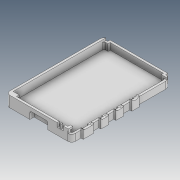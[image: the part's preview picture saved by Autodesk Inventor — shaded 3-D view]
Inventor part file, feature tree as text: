
AUTODESK INVENTOR PART (.ipt)
format: ipt  version: 2020 (Build 240168000, 168)  size: 389,120 bytes
history: native  units: mm
features: extrude x11, sketch x10
ambient origin geometry x8: Origin, YZ Plane, XZ Plane, XY Plane, X Axis, Y Axis, Z Axis, Center Point
bodies: Solid1 (feature_tree)
feature tree (21):
  extrude  "Extrusion1"  Depth=60.0mm
  extrude  "Extrusion2"  Depth=2.0mm
  extrude  "Extrusion3"  Depth=2.0mm TaperAngle=0.0deg
  extrude  "Extrusion4"  Depth=9.6mm
  extrude  "Extrusion5"  Depth=1.0mm
  extrude  "Extrusion6"  Depth=6.7mm
  extrude  "Extrusion7"  Depth=1.5mm
  extrude  "Extrusion8"  Depth=6.7mm
  extrude  "Extrusion12"  Depth=1.0mm
  sketch  "Sketch12"  dims[d19=7.6mm d20=6.7mm d21=9.0mm d22=8.0mm d23=2.0mm d24=0.0mm d25=2.0mm d27=2.0mm d28=2.5mm d29=2.5mm d30=2.5mm d31=5.5mm d32=4.3mm d33=0.0mm d35=2.0mm d36=2.0mm d37=6.0mm d38=0.0mm d39=2.0mm d40=8.0mm d41=0.0mm d42=7.5mm d43=4.5mm d44=1.5mm d45=0.0mm d46=2.3mm d47=4.2mm d48=4.2mm d49=2.0mm d50=3.0mm d51=1.5mm d52=0.0mm d53=2.3mm d55=2.3mm d56=1.0mm d57=2.3mm d58=1.5mm d59=0.0mm d71=6.8mm d72=16.4mm d73=1.5mm d74=3.8mm d75=0.0mm d76=1.0mm d77=4.8mm d78=2.0mm d79=0.0mm d80=3.0mm d81=0.0mm]
  extrude  "Extrusion13"  Depth=6.7mm
  extrude  "Extrusion14"  Depth=3.0mm
  sketch  "Sketch1"  dims[d0=89.7mm d1=60.0mm]
  sketch  "Sketch2"  dims[d2=3.5mm d3=2.0mm]
  sketch  "Sketch3"  dims[d4=52.8mm d5=2.0mm d6=0.0mm]
  sketch  "Sketch4"  dims[d7=8.0mm d8=9.6mm]
  sketch  "Sketch5"  dims[d9=8.6mm d10=1.0mm]
  sketch  "Sketch6"  dims[d11=1.5mm d12=6.7mm]
  sketch  "Sketch7"  dims[d13=7.0mm d14=1.5mm]
  sketch  "Sketch8"  dims[d15=1.0mm d16=6.7mm]
  sketch  "Sketch11"  dims[d17=1.5mm d18=1.0mm]
